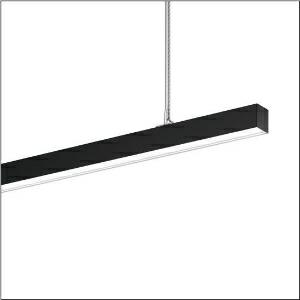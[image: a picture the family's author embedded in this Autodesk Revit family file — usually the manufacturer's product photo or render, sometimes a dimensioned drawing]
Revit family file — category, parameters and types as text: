
# Revit family: silica_r__21_51mx30tat4b_500a
name_source: partatom
category: Lighting Fixtures
units: mm (PartAtom-declared; Revit-internal decimal feet)

## family parameters
Cut with Voids When Loaded = No
Host = Face
Light Source = No
Part Type = Normal
Room Calculation Point = No
Round Connector Dimension = Use Diameter
Shared = No

## types (1)
- --- (1 x LED, 4120 lm, 33.8 W, 6500K)
    Apparent Load = 34 VA
    CIE Flux Codes = 47 79 96 58 100
    Color Rendering = 80
    Color Temperature = 6500K
    Default Elevation = 1800 mm
    Description = Silica® 21, office luminaire, primary optical cover: cover, of PMMA, opal, light emission: direct/indirect distribution, primary light characteristic: symmetric, installation type: suspended mounting, LED, rated luminous flux: 4.120lm, luminous efficacy: 116lm/W, light colour: 8tw, colour temperature: 2700..6500K, control gear: DALI DT8, with terminal, 3+2-pole, max. 2.5mm², mains connection: 220..240V, AC, 50/60Hz, rated input power: 35.5W, luminaire housing, of aluminium, matt jet black (RAL 9005), length: 1.204mm, width: 53mm, height: 53mm, protection rating (complete): IP20, insulation class (complete): insulation class I (protective earthing), certification: CE, permissible operating ambient temperature: 0..+35°C, standard: EN 50419, packaging unit: 1 piece
    Height = 53 mm
    Lamp = 1 x LED
    Lamp Light Flux = 4120 lm
    Lamp Power = 33.8 W
    Lamp count = 1
    Length = 1204 mm
    Luminous efficacy = 122 lm/W
    Manufacturer = Siteco
    ModVariant = No
    Model = 51MX30TAT4B
    Mounting Place = Ceiling
    Mounting Type = Pendant
    Number of Poles = 1
    OnlyDefault = Yes
    Power Factor = 1
    Product Name = Silica® 21
    Product group = office luminaire | ceiling pendant
    ProductGroupID = 904
    Protection Class = Protection class I
    Protection Degree = IP 20
    RLX_Detail_Level = 1
    RLX_Emergency_Light_Flux = 0 lm
    RLX_Emergency_Type = 0
    RLX_Emergency_Type_DB = No
    RlxData = <blob elided: 22849 chars, md5=9e8b40ec>
    Socket = socket
    Standby Power = 0 W
    System Light Flux = 4120 lm
    System Power = 34 W
    Type Comments = individual setting
    Type Image = l_1335856.jpg
    URL = http://relux.com
    VarID = @adj_139638
    Voltage = 0 V
    Weight = 0.00 kg
    Width = 53 mm

## geometry (parser evidence)
native form markers: Blend x4, Sweep x11
no freeform markers — native parametric forms only
